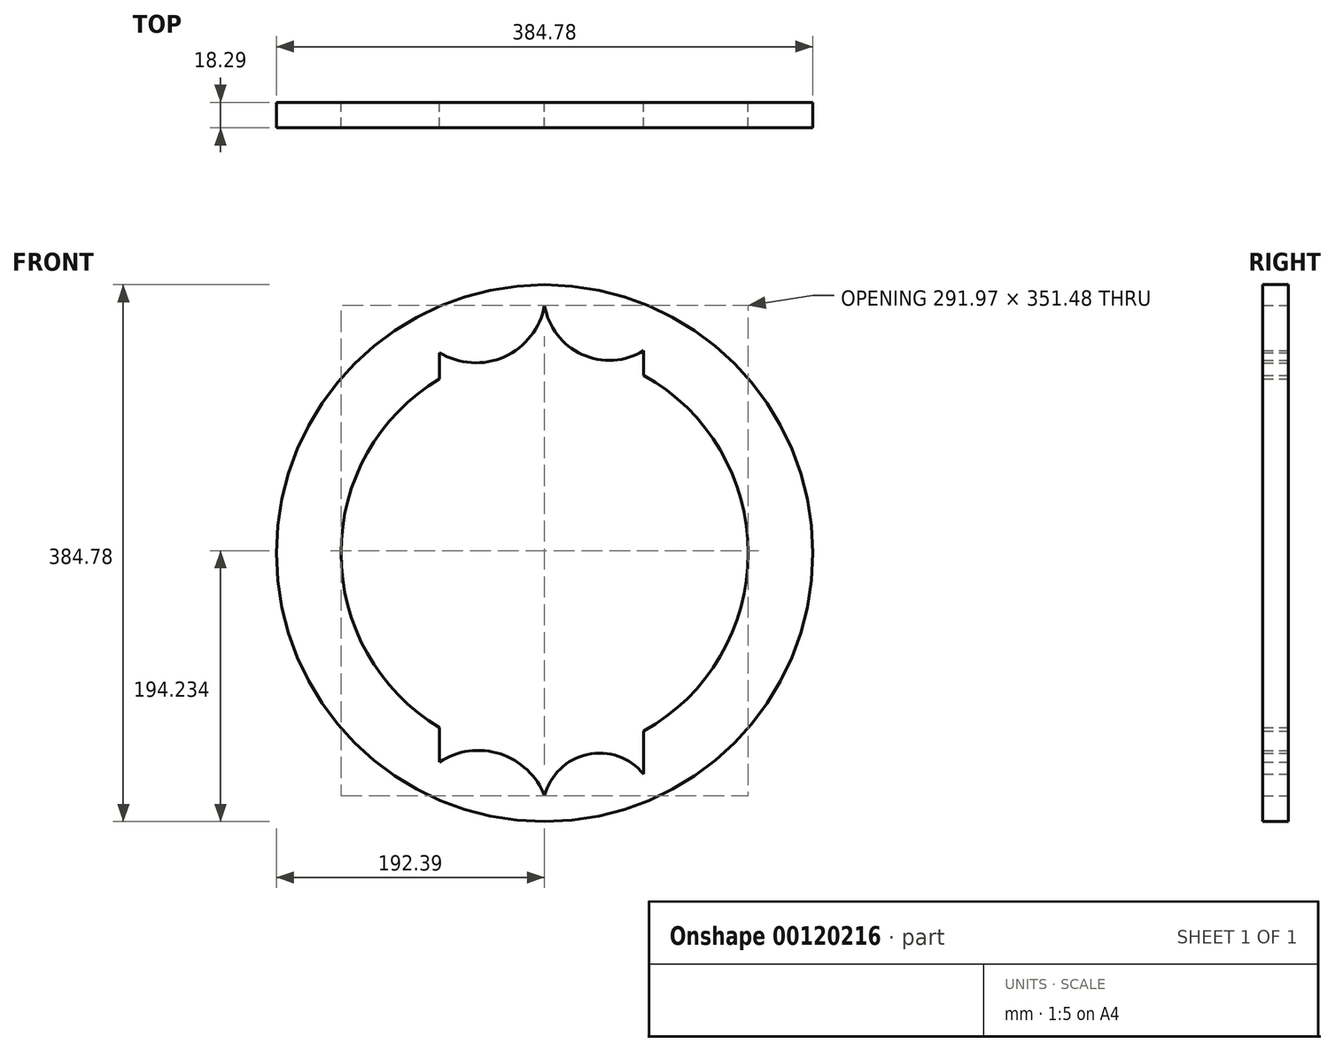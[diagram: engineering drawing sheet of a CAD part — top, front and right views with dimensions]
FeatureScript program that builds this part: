
annotation { "Feature Type Name" : "Feature", "Feature Type Description" : "" }
export const myFeature = defineFeature(function(context is Context, id is Id, definition is map)
    precondition{}
    {
        {
            var Q0;
            Q0=qCreatedBy(makeId("Front.planeOp"),FACE);
            var sketch = newSketch(context, id + "F0", { "sketchPlane" : qUnion([Q0])});
            skCircle(sketch, "E0", {"center": v(0, 0) * mm, "radius": 192.4 * mm});
            skArc(sketch, "E1", {"start": v(-75.42, 124.99) * mm, "mid": v(-145.98, 0) * mm, "end": v(-75.42, -124.99) * mm});
            skLineSegment(sketch, "E2", {"start": v(-75.42, 124.99) * mm, "end": v(-75.42, 143.76) * mm});
            skLineSegment(sketch, "E3", {"start": v(71.05, 145.23) * mm, "end": v(71.05, 127.52) * mm});
            skArc(sketch, "E4", {"start": v(-75.42, 143.76) * mm, "mid": v(-28.81, 140.83) * mm, "end": v(0, 177.58) * mm});
            skArc(sketch, "E5", {"start": v(0, 177.58) * mm, "mid": v(26.87, 142.39) * mm, "end": v(71.05, 145.23) * mm});
            skLineSegment(sketch, "E6", {"start": v(-75.42, -124.99) * mm, "end": v(-75.42, -149.63) * mm});
            skLineSegment(sketch, "E7", {"start": v(71.05, -158.45) * mm, "end": v(71.05, -150.18) * mm});
            skArc(sketch, "E8.trimOffspring", {"start": v(71.05, -127.52) * mm, "mid": v(145.98, 0) * mm, "end": v(71.05, 127.52) * mm});
            skLineSegment(sketch, "E9", {"start": v(71.05, -150.18) * mm, "end": v(71.05, -127.52) * mm});
            skArc(sketch, "E10", {"start": v(0, -173.9) * mm, "mid": v(-31.94, -143.82) * mm, "end": v(-75.42, -149.63) * mm});
            skArc(sketch, "E11", {"start": v(71.05, -158.45) * mm, "mid": v(30.75, -144.19) * mm, "end": v(0, -173.9) * mm});
            skLineSegment(sketch, "E12", {"start": v(133.26, 59.61) * mm, "end": v(133.26, 59.61) * mm});
            skPoint(sketch, "E13.center.orphan", {"position": v(-129.4, -67.57) * mm});
            skPoint(sketch, "E14.center.orphan", {"position": v(129.4, -67.57) * mm});
            skSolve(sketch);
        }
        {
            var Q0;
            Q0 = qSketchRegion(id + "F0", true);
            extrude(context, id + "F1", {"entities" : qUnion([Q0]), "depth" : 18.3 * mm});
        }
    });
